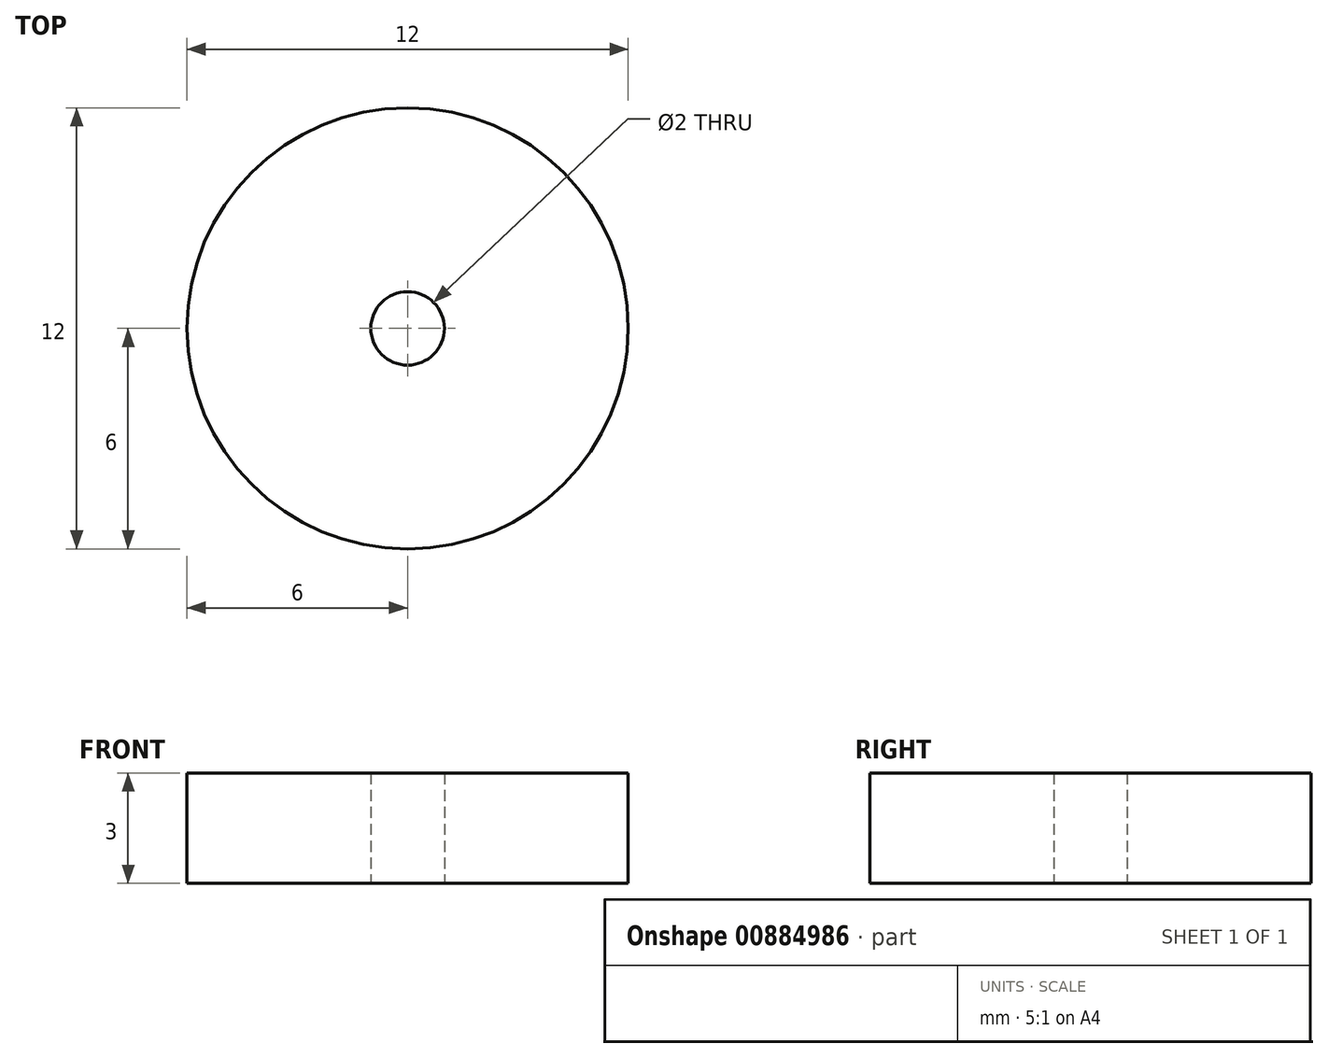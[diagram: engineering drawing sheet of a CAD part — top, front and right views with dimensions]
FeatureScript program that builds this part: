
annotation { "Feature Type Name" : "Feature", "Feature Type Description" : "" }
export const myFeature = defineFeature(function(context is Context, id is Id, definition is map)
    precondition{}
    {
        {
            var Q0;
            Q0=qCreatedBy(makeId("Top.planeOp"),FACE);
            var sketch = newSketch(context, id + "F0", { "sketchPlane" : qUnion([Q0])});
            skCircle(sketch, "E0", {"center": v(0, 0) * mm, "radius": 6 * mm});
            skCircle(sketch, "E1", {"center": v(0, 0) * mm, "radius": 1 * mm});
            skSolve(sketch);
        }
        {
            var Q0;
            Q0=makeQuery(id+"F0.imprint","IMPRINT",FACE,{"disambiguationData":[TD([[makeQuery(id+"F0.imprint","IMPRINT",EDGE,{"derivedFrom":sQuery(id+"F0.wireOp",EDGE,"E0")}),1.0]])]});
            extrude(context, id + "F1", {"entities" : qUnion([Q0]), "depth" : 3 * mm, "offsetDistance" : 25 * mm});
        }
    });
